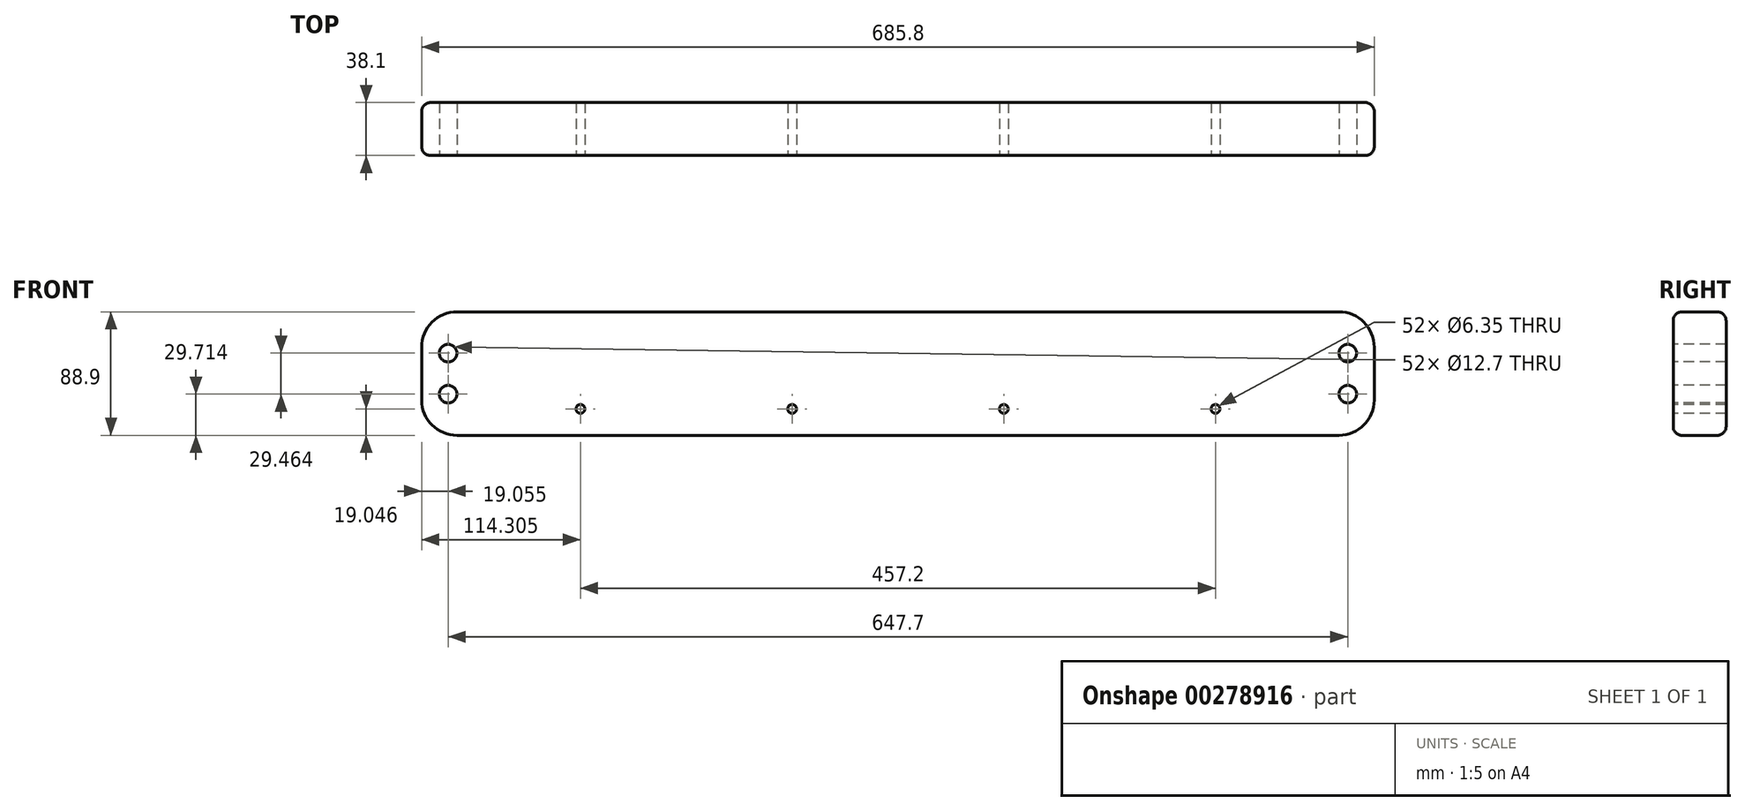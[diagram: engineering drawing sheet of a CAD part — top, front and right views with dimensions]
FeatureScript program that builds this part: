
annotation { "Feature Type Name" : "Feature", "Feature Type Description" : "" }
export const myFeature = defineFeature(function(context is Context, id is Id, definition is map)
    precondition{}
    {
        {
            var Q0;
            Q0=qCreatedBy(makeId("Front.planeOp"),FACE);
            var sketch = newSketch(context, id + "F0", { "sketchPlane" : qUnion([Q0])});
            skLineSegment(sketch, "E0.bottom", {"start": v(-166, -25.44) * mm, "end": v(519.8, -25.44) * mm});
            skLineSegment(sketch, "E0.top", {"start": v(-166, 63.46) * mm, "end": v(519.8, 63.46) * mm});
            skLineSegment(sketch, "E0.left", {"start": v(-166, -25.44) * mm, "end": v(-166, 63.46) * mm});
            skLineSegment(sketch, "E0.right", {"start": v(519.8, -25.44) * mm, "end": v(519.8, 63.46) * mm});
            skCircle(sketch, "E1", {"center": v(-146.96, 33.74) * mm, "radius": 6.35 * mm});
            skCircle(sketch, "E2", {"center": v(-146.96, 4.27) * mm, "radius": 6.35 * mm});
            skCircle(sketch, "E3", {"center": v(500.74, 33.74) * mm, "radius": 6.35 * mm});
            skCircle(sketch, "E4", {"center": v(500.74, 4.27) * mm, "radius": 6.35 * mm});
            skCircle(sketch, "E5", {"center": v(-51.7, -6.4) * mm, "radius": 3.18 * mm});
            skCircle(sketch, "E6.1.0.0", {"center": v(100.7, -6.4) * mm, "radius": 3.18 * mm});
            skCircle(sketch, "E6.2.0.0", {"center": v(253.1, -6.4) * mm, "radius": 3.18 * mm});
            skCircle(sketch, "E6.3.0.0", {"center": v(405.5, -6.4) * mm, "radius": 3.18 * mm});
            skLineSegment(sketch, "E6.direction1", {"start": v(-51.7, -6.4) * mm, "end": v(100.7, -6.4) * mm, "construction": true});
            skSolve(sketch);
        }
        {
            var Q0;
            Q0=qSketchRegion(id+"F0",true);
            extrude(context, id + "F1", {"entities" : qUnion([Q0]), "oppositeDirection" : true, "depth" : 38.1 * mm});
        }
        {
            var Q0;
            Q0=makeQuery(id+"F1.opExtrude","SWEPT_EDGE",EDGE,{"disambiguationData":[OSD([sQuery(id+"F0.wireOp",EDGE,"E0.top"),sQuery(id+"F0.wireOp",EDGE,"E0.right")])]});
            var Q1;
            Q1=makeQuery(id+"F1.opExtrude","SWEPT_EDGE",EDGE,{"disambiguationData":[OSD([sQuery(id+"F0.wireOp",EDGE,"E0.bottom"),sQuery(id+"F0.wireOp",EDGE,"E0.right")])]});
            var Q2;
            Q2=makeQuery(id+"F1.opExtrude","SWEPT_EDGE",EDGE,{"disambiguationData":[OSD([sQuery(id+"F0.wireOp",EDGE,"E0.top"),sQuery(id+"F0.wireOp",EDGE,"E0.left")])]});
            var Q3;
            Q3=makeQuery(id+"F1.opExtrude","SWEPT_EDGE",EDGE,{"disambiguationData":[OSD([sQuery(id+"F0.wireOp",EDGE,"E0.bottom"),sQuery(id+"F0.wireOp",EDGE,"E0.left")])]});
            fillet(context, id + "F2", {"entities" : qUnion([Q0, Q1, Q2, Q3]), "radius" : 25.4 * mm, "tangentPropagation" : true, "allowEdgeOverflow" : false});
        }
        {
            var Q0;
            Q0=makeQuery(id+"F1.opExtrude","CAP_EDGE",EDGE,{"disambiguationData":[OSD([sQuery(id+"F0.wireOp",EDGE,"E0.top")])],"isStart":true});
            var Q1;
            Q1=makeQuery(id+"F1.opExtrude","CAP_EDGE",EDGE,{"disambiguationData":[OSD([sQuery(id+"F0.wireOp",EDGE,"E0.top")])],"isStart":false});
            fillet(context, id + "F3", {"entities" : qUnion([Q0, Q1]), "radius" : 6.35 * mm, "tangentPropagation" : true, "allowEdgeOverflow" : false});
        }
    });
